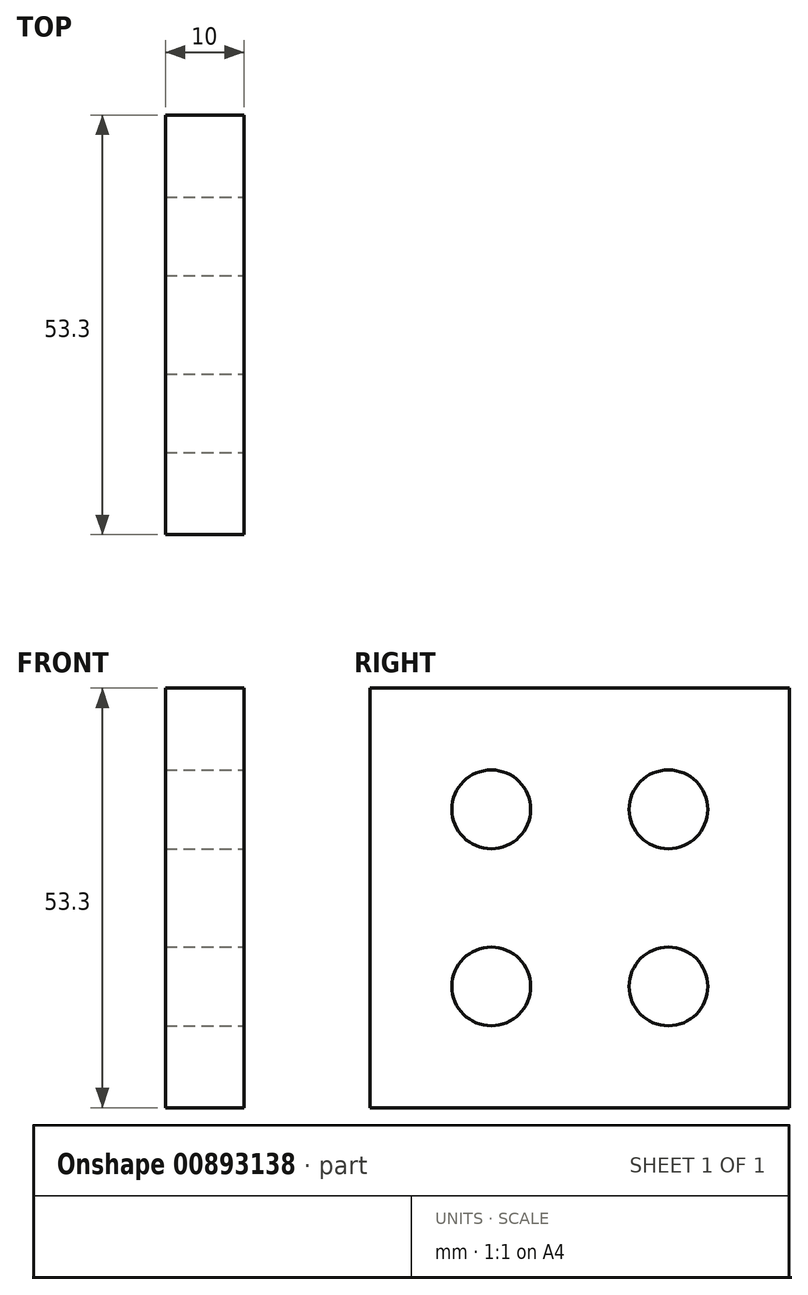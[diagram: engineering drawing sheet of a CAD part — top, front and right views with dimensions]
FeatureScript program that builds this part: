
annotation { "Feature Type Name" : "Feature", "Feature Type Description" : "" }
export const myFeature = defineFeature(function(context is Context, id is Id, definition is map)
    precondition{}
    {
        {
            var Q0;
            Q0=qCreatedBy(makeId("Right.planeOp"),FACE);
            var sketch = newSketch(context, id + "F0", { "sketchPlane" : qUnion([Q0])});
            skCircle(sketch, "E0", {"center": v(0, 0) * mm, "radius": 5 * mm});
            skCircle(sketch, "E1", {"center": v(0, 22.5) * mm, "radius": 5 * mm});
            skCircle(sketch, "E2.MirrorC", {"center": v(22.5, 22.5) * mm, "radius": 5 * mm});
            skCircle(sketch, "E3.MirrorC", {"center": v(22.5, 0) * mm, "radius": 5 * mm});
            skPoint(sketch, "E4.endSnap0", {"position": v(3.75, 0) * mm});
            skPoint(sketch, "E4.endSnap1", {"position": v(0, 3.75) * mm});
            skPoint(sketch, "E5.endSnap0", {"position": v(3.75, 22.5) * mm});
            skLineSegment(sketch, "E6.0", {"start": v(0, 37.9) * mm, "end": v(22.5, 37.9) * mm});
            skLineSegment(sketch, "E7.0", {"start": v(22.5, -15.4) * mm, "end": v(0, -15.4) * mm});
            skLineSegment(sketch, "E8.0", {"start": v(-15.4, 15) * mm, "end": v(-15.4, 7.5) * mm});
            skLineSegment(sketch, "E9.0", {"start": v(37.9, 22.5) * mm, "end": v(37.9, 0) * mm});
            skLineSegment(sketch, "E10", {"start": v(22.5, 37.9) * mm, "end": v(37.9, 37.9) * mm});
            skLineSegment(sketch, "E11", {"start": v(37.9, 37.9) * mm, "end": v(37.9, 22.5) * mm});
            skLineSegment(sketch, "E12", {"start": v(0, 37.9) * mm, "end": v(-15.4, 37.9) * mm});
            skLineSegment(sketch, "E13", {"start": v(-15.4, 37.9) * mm, "end": v(-15.4, 15) * mm});
            skLineSegment(sketch, "E14", {"start": v(0, -15.4) * mm, "end": v(-15.4, -15.4) * mm});
            skLineSegment(sketch, "E15", {"start": v(-15.4, -15.4) * mm, "end": v(-15.4, 7.5) * mm});
            skLineSegment(sketch, "E16", {"start": v(22.5, -15.4) * mm, "end": v(37.9, -15.4) * mm});
            skLineSegment(sketch, "E17", {"start": v(37.9, -15.4) * mm, "end": v(37.9, 0) * mm});
            skSolve(sketch);
        }
        {
            var Q0;
            Q0=makeQuery(id+"F0.imprint","IMPRINT",FACE,{"disambiguationData":[TD([[makeQuery(id+"F0.imprint","IMPRINT",EDGE,{"derivedFrom":sQuery(id+"F0.wireOp",EDGE,"E0")}),-1.0]])]});
            extrude(context, id + "F1", {"entities" : qUnion([Q0]), "oppositeDirection" : true, "depth" : 10 * mm, "offsetDistance" : 25 * mm});
        }
    });
